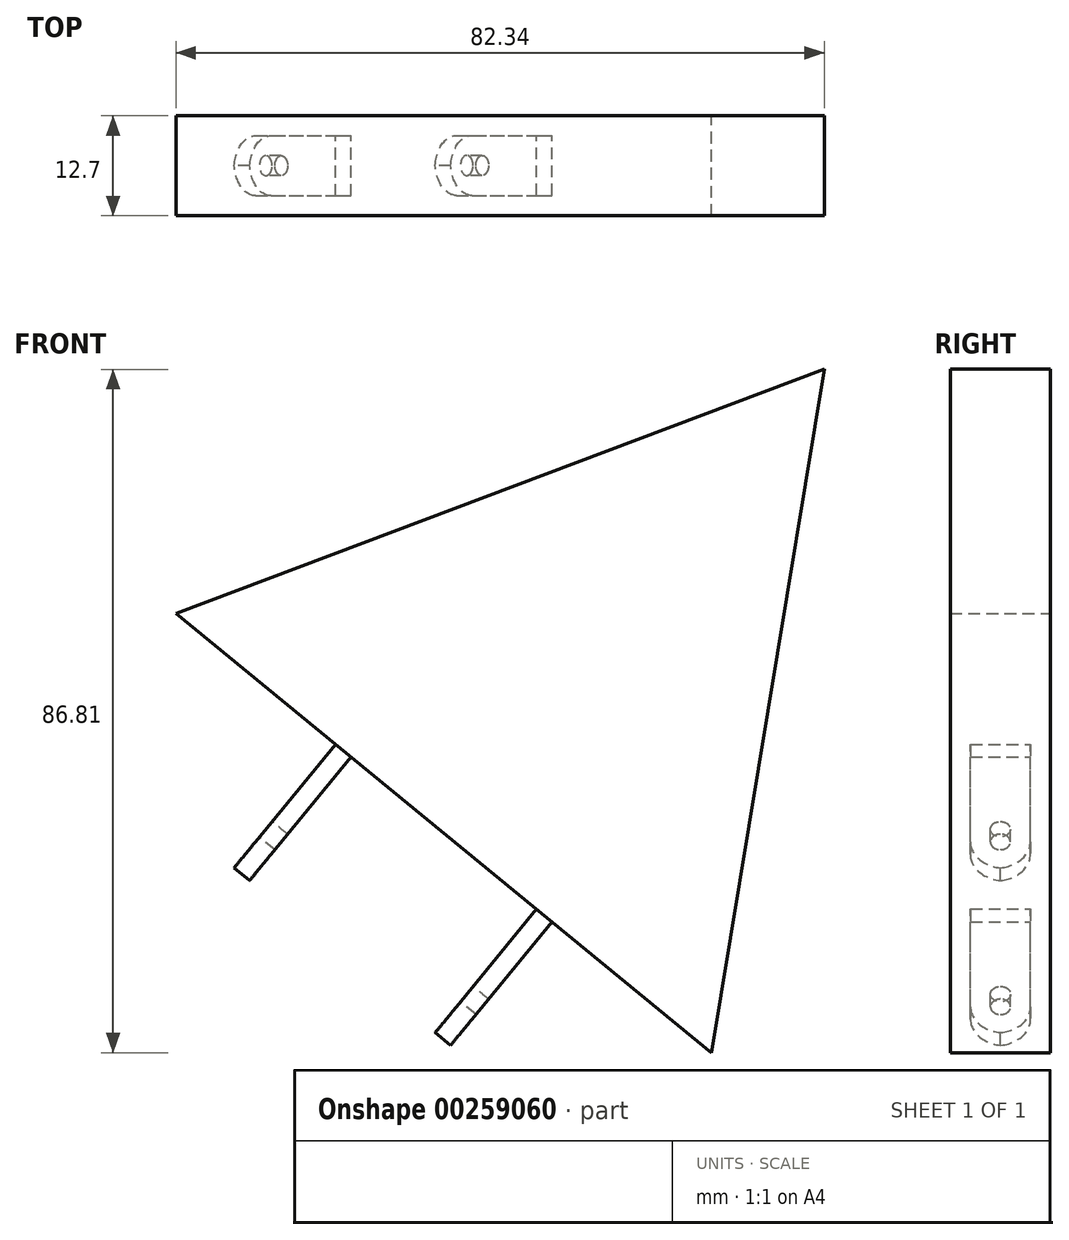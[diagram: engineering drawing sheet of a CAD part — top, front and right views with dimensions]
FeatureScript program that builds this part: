
annotation { "Feature Type Name" : "Feature", "Feature Type Description" : "" }
export const myFeature = defineFeature(function(context is Context, id is Id, definition is map)
    precondition{}
    {
        {
            var Q0;
            Q0=qCreatedBy(makeId("Front.planeOp"),FACE);
            var sketch = newSketch(context, id + "F0", { "sketchPlane" : qUnion([Q0])});
            skCircle(sketch, "E0.cCircle", {"center": v(0, 0) * mm, "radius": 25.4 * mm, "construction": true});
            skLineSegment(sketch, "E0.0", {"start": v(-50.12, 8.27) * mm, "end": v(32.22, 39.27) * mm});
            skLineSegment(sketch, "E0.1", {"start": v(32.22, 39.27) * mm, "end": v(17.9, -47.54) * mm});
            skLineSegment(sketch, "E0.2", {"start": v(17.9, -47.54) * mm, "end": v(-50.12, 8.27) * mm});
            skPoint(sketch, "E0.0.midPoint", {"position": v(-8.95, 23.77) * mm});
            skSolve(sketch);
        }
        {
            var Q0;
            Q0 = qSketchRegion(id + "F0", true);
            extrude(context, id + "F1", {"entities" : qUnion([Q0]), "depth" : 12.7 * mm});
        }
        {
            var Q0;
            Q0=makeQuery(id+"F1.opExtrude","SWEPT_FACE",FACE,{"disambiguationData":[OSD([sQuery(id+"F0.wireOp",EDGE,"E0.2")])]});
            var sketch = newSketch(context, id + "F2", { "sketchPlane" : qUnion([Q0])});
            skLineSegment(sketch, "E1", {"start": v(0, 12.7) * mm, "end": v(0, 0) * mm, "construction": true});
            skLineSegment(sketch, "E2.bottom", {"start": v(-17.78, 10.14) * mm, "end": v(-15.24, 10.14) * mm});
            skLineSegment(sketch, "E2.top", {"start": v(-17.78, 2.52) * mm, "end": v(-15.24, 2.52) * mm});
            skLineSegment(sketch, "E2.left", {"start": v(-17.78, 10.14) * mm, "end": v(-17.78, 2.52) * mm});
            skLineSegment(sketch, "E2.right", {"start": v(-15.24, 10.14) * mm, "end": v(-15.24, 2.52) * mm});
            skLineSegment(sketch, "E3.bottom", {"start": v(15.24, 10.11) * mm, "end": v(17.78, 10.11) * mm});
            skLineSegment(sketch, "E3.top", {"start": v(15.24, 2.5) * mm, "end": v(17.78, 2.5) * mm});
            skLineSegment(sketch, "E3.left", {"start": v(15.24, 10.11) * mm, "end": v(15.24, 2.5) * mm});
            skLineSegment(sketch, "E3.right", {"start": v(17.78, 10.11) * mm, "end": v(17.78, 2.5) * mm});
            skSolve(sketch);
        }
        {
            var Q0;
            Q0 = qSketchRegion(id + "F2", true);
            var Q1;
            Q1 = qConstructionFilter(qBodyType(qCreatedBy(id + "F2" ,EDGE), BodyType.WIRE), ConstructionObject.NO);
            extrude(context, id + "F3", {"entities" : qUnion([Q0]), "operationType" : NewBodyOperationType.ADD, "surfaceEntities" : qUnion([Q1]), "depth" : 20.32 * mm});
        }
        {
            var Q0;
            Q0=makeQuery(id+"F3.opExtrude","SWEPT_FACE",FACE,{"disambiguationData":[OSD([sQuery(id+"F2.wireOp",EDGE,"E2.left")])]});
            var sketch = newSketch(context, id + "F4", { "sketchPlane" : qUnion([Q0])});
            skLineSegment(sketch, "E4.bottom", {"start": v(10.14, -45.72) * mm, "end": v(2.52, -45.72) * mm, "construction": true});
            skLineSegment(sketch, "E4.top", {"start": v(10.14, -33.02) * mm, "end": v(2.52, -33.02) * mm, "construction": true});
            skLineSegment(sketch, "E4.left", {"start": v(10.14, -45.72) * mm, "end": v(10.14, -33.02) * mm, "construction": true});
            skLineSegment(sketch, "E4.right", {"start": v(2.52, -45.72) * mm, "end": v(2.52, -33.02) * mm, "construction": true});
            skLineSegment(sketch, "E5", {"start": v(10.14, -45.72) * mm, "end": v(2.52, -33.02) * mm, "construction": true});
            skLineSegment(sketch, "E6", {"start": v(10.14, -33.02) * mm, "end": v(2.52, -45.72) * mm, "construction": true});
            skCircle(sketch, "E7", {"center": v(6.33, -39.37) * mm, "radius": 1.27 * mm});
            skSolve(sketch);
        }
        {
            var Q0;
            Q0 = qSketchRegion(id + "F4", true);
            extrude(context, id + "F5", {"entities" : qUnion([Q0]), "operationType" : NewBodyOperationType.REMOVE, "oppositeDirection" : true, "depth" : 25.4 * mm});
        }
        {
            var Q0;
            Q0=makeQuery(id+"F3.opExtrude","SWEPT_FACE",FACE,{"disambiguationData":[OSD([sQuery(id+"F2.wireOp",EDGE,"E3.left")])]});
            var sketch = newSketch(context, id + "F6", { "sketchPlane" : qUnion([Q0])});
            skLineSegment(sketch, "E8.bottom", {"start": v(10.11, -45.72) * mm, "end": v(2.5, -45.72) * mm, "construction": true});
            skLineSegment(sketch, "E8.top", {"start": v(10.11, -33.02) * mm, "end": v(2.5, -33.02) * mm, "construction": true});
            skLineSegment(sketch, "E8.left", {"start": v(10.11, -45.72) * mm, "end": v(10.11, -33.02) * mm, "construction": true});
            skLineSegment(sketch, "E8.right", {"start": v(2.5, -45.72) * mm, "end": v(2.5, -33.02) * mm, "construction": true});
            skLineSegment(sketch, "E9", {"start": v(10.11, -45.72) * mm, "end": v(2.5, -33.02) * mm, "construction": true});
            skLineSegment(sketch, "E10", {"start": v(10.11, -33.02) * mm, "end": v(2.5, -45.72) * mm, "construction": true});
            skCircle(sketch, "E11", {"center": v(6.3, -39.37) * mm, "radius": 1.27 * mm});
            skSolve(sketch);
        }
        {
            var Q0;
            Q0 = qSketchRegion(id + "F6", true);
            extrude(context, id + "F7", {"entities" : qUnion([Q0]), "operationType" : NewBodyOperationType.REMOVE, "oppositeDirection" : true, "depth" : 25.4 * mm});
        }
        {
            var Q0;
            Q0=makeQuery(id+"F3.opExtrude","CAP_EDGE",EDGE,{"disambiguationData":[OSD([sQuery(id+"F2.wireOp",EDGE,"E2.top")])],"isStart":false});
            var Q1;
            Q1=makeQuery(id+"F3.opExtrude","CAP_EDGE",EDGE,{"disambiguationData":[OSD([sQuery(id+"F2.wireOp",EDGE,"E2.bottom")])],"isStart":false});
            var Q2;
            Q2=makeQuery(id+"F3.opExtrude","CAP_EDGE",EDGE,{"disambiguationData":[OSD([sQuery(id+"F2.wireOp",EDGE,"E3.top")])],"isStart":false});
            var Q3;
            Q3=makeQuery(id+"F3.opExtrude","CAP_EDGE",EDGE,{"disambiguationData":[OSD([sQuery(id+"F2.wireOp",EDGE,"E3.bottom")])],"isStart":false});
            fillet(context, id + "F8", {"entities" : qUnion([Q0, Q1, Q2, Q3]), "radius" : 4.3 * mm, "tangentPropagation" : true, "allowEdgeOverflow" : false});
        }
    });
